annotation { "Feature Type Name" : "Feature", "Feature Type Description" : "" }
export const myFeature = defineFeature(function(context is Context, id is Id, definition is map)
    precondition{}
    {
        {
            var Q0;
            Q0=qCreatedBy(makeId("Top.planeOp"),FACE);
            var sketch = newSketch(context, id + "F0", { "sketchPlane" : qUnion([Q0])});
            skLineSegment(sketch, "E0.bottom", {"start": v(-93.3, 45.8) * mm, "end": v(93.3, 45.8) * mm});
            skLineSegment(sketch, "E0.top", {"start": v(-93.3, -45.8) * mm, "end": v(93.3, -45.8) * mm});
            skLineSegment(sketch, "E0.left", {"start": v(-103.3, 35.8) * mm, "end": v(-103.3, -35.8) * mm});
            skLineSegment(sketch, "E0.right", {"start": v(103.3, 35.8) * mm, "end": v(103.3, -35.8) * mm});
            skPoint(sketch, "E1", {"position": v(-103.3, 0) * mm});
            skPoint(sketch, "E2", {"position": v(0, 45.8) * mm});
            skPoint(sketch, "E3.visualSharp", {"position": v(-103.3, 45.8) * mm});
            skArc(sketch, "E3.filletArc", {"start": v(-93.3, 45.8) * mm, "mid": v(-100.37, 42.87) * mm, "end": v(-103.3, 35.8) * mm});
            skPoint(sketch, "E4.visualSharp", {"position": v(103.3, 45.8) * mm});
            skArc(sketch, "E4.filletArc", {"start": v(103.3, 35.8) * mm, "mid": v(100.37, 42.87) * mm, "end": v(93.3, 45.8) * mm});
            skPoint(sketch, "E5.visualSharp", {"position": v(103.3, -45.8) * mm});
            skArc(sketch, "E5.filletArc", {"start": v(93.3, -45.8) * mm, "mid": v(100.37, -42.87) * mm, "end": v(103.3, -35.8) * mm});
            skPoint(sketch, "E6.visualSharp", {"position": v(-103.3, -45.8) * mm});
            skArc(sketch, "E6.filletArc", {"start": v(-103.3, -35.8) * mm, "mid": v(-100.37, -42.87) * mm, "end": v(-93.3, -45.8) * mm});
            skSolve(sketch);
        }
        {
            var Q0;
            Q0=qCreatedBy(makeId("Top.planeOp"),FACE);
            var sketch = newSketch(context, id + "F1", { "sketchPlane" : qUnion([Q0])});
            skLineSegment(sketch, "E7", {"start": v(-42.83, 13.32) * mm, "end": v(-36.1, 13.32) * mm});
            skLineSegment(sketch, "E8", {"start": v(-36.1, 13.32) * mm, "end": v(-39.45, -1.37) * mm});
            skLineSegment(sketch, "E9", {"start": v(-42.83, 13.32) * mm, "end": v(-46.01, -0.65) * mm});
            skLineSegment(sketch, "E10", {"start": v(-45.48, 8.48) * mm, "end": v(-46.34, 4.71) * mm});
            skLineSegment(sketch, "E11", {"start": v(-53.53, -1.78) * mm, "end": v(-47.43, -1.78) * mm});
            skLineSegment(sketch, "E12", {"start": v(-54.43, -0.65) * mm, "end": v(-53.38, 4) * mm});
            skLineSegment(sketch, "E13", {"start": v(-46.34, 4.71) * mm, "end": v(-52.47, 4.71) * mm});
            skLineSegment(sketch, "E14", {"start": v(-45.48, 8.48) * mm, "end": v(-55.95, 8.48) * mm});
            skLineSegment(sketch, "E15", {"start": v(-44.42, -5.34) * mm, "end": v(-60, -5.34) * mm});
            skLineSegment(sketch, "E16", {"start": v(-60.83, 4.59) * mm, "end": v(-62.4, -2.33) * mm});
            skPoint(sketch, "E17.orphan", {"position": v(-46.57, -3.1) * mm});
            skPoint(sketch, "E18.visualSharp", {"position": v(-59.94, 8.48) * mm});
            skArc(sketch, "E18.filletArc", {"start": v(-55.95, 8.48) * mm, "mid": v(-59.07, 7.38) * mm, "end": v(-60.83, 4.59) * mm});
            skPoint(sketch, "E19.visualSharp", {"position": v(-40.35, -5.34) * mm});
            skArc(sketch, "E19.filletArc", {"start": v(-44.42, -5.34) * mm, "mid": v(-41.24, -4.23) * mm, "end": v(-39.45, -1.37) * mm});
            skPoint(sketch, "E20.visualSharp", {"position": v(-63.09, -5.34) * mm});
            skArc(sketch, "E20.filletArc", {"start": v(-62.4, -2.33) * mm, "mid": v(-61.93, -4.41) * mm, "end": v(-60, -5.34) * mm});
            skPoint(sketch, "E21.visualSharp", {"position": v(-54.7, -1.78) * mm});
            skArc(sketch, "E21.filletArc", {"start": v(-54.43, -0.65) * mm, "mid": v(-54.25, -1.43) * mm, "end": v(-53.53, -1.78) * mm});
            skPoint(sketch, "E22.visualSharp", {"position": v(-46.27, -1.78) * mm});
            skArc(sketch, "E22.filletArc", {"start": v(-47.43, -1.78) * mm, "mid": v(-46.52, -1.47) * mm, "end": v(-46.01, -0.65) * mm});
            skPoint(sketch, "E23.visualSharp", {"position": v(-53.21, 4.71) * mm});
            skArc(sketch, "E23.filletArc", {"start": v(-52.47, 4.71) * mm, "mid": v(-53.05, 4.51) * mm, "end": v(-53.38, 4) * mm});
            skLineSegment(sketch, "E24", {"start": v(-35.57, 8.44) * mm, "end": v(-29.1, 8.44) * mm});
            skLineSegment(sketch, "E25", {"start": v(-24.17, -5.38) * mm, "end": v(-30.7, -5.38) * mm});
            skLineSegment(sketch, "E26", {"start": v(-47.3, -6.65) * mm, "end": v(-42.86, -6.65) * mm});
            skLineSegment(sketch, "E27", {"start": v(-48.81, -11.27) * mm, "end": v(-39.5, -11.27) * mm});
            skLineSegment(sketch, "E28", {"start": v(-35.57, 8.44) * mm, "end": v(-38.1, -2.84) * mm});
            skLineSegment(sketch, "E29", {"start": v(-29.1, 8.44) * mm, "end": v(-32.2, -5.43) * mm});
            skLineSegment(sketch, "E30", {"start": v(-47.3, -6.65) * mm, "end": v(-48.81, -11.27) * mm});
            skLineSegment(sketch, "E31", {"start": v(-27.6, 8.44) * mm, "end": v(-30.7, -5.38) * mm});
            skLineSegment(sketch, "E32", {"start": v(-24.17, -5.38) * mm, "end": v(-21.08, 8.44) * mm});
            skLineSegment(sketch, "E33.trimOffspring", {"start": v(-27.6, 8.44) * mm, "end": v(-21.08, 8.44) * mm});
            skPoint(sketch, "E34.visualSharp", {"position": v(-33.5, -11.27) * mm});
            skArc(sketch, "E34.filletArc", {"start": v(-39.5, -11.27) * mm, "mid": v(-34.82, -9.63) * mm, "end": v(-32.2, -5.43) * mm});
            skPoint(sketch, "E35.visualSharp", {"position": v(-38.95, -6.65) * mm});
            skArc(sketch, "E35.filletArc", {"start": v(-42.86, -6.65) * mm, "mid": v(-39.8, -5.58) * mm, "end": v(-38.1, -2.84) * mm});
            skLineSegment(sketch, "E36", {"start": v(0, 46.06) * mm, "end": v(0, -46.43) * mm, "construction": true});
            skText(sketch, "E37", { "text": "MAVIC PRO", "fontName": "OpenSans-Regular.ttf"});
            const initialGuessF1  = {"E37": [-0.00124, -0.00387, 1, 0, 0.008]};
            skSetInitialGuess(sketch, initialGuessF1);
            skSolve(sketch);
        }
        {
            var Q0;
            Q0=makeQuery(id+"F0.imprint","IMPRINT",FACE,{"disambiguationData":[TD([[makeQuery(id+"F0.imprint","IMPRINT",EDGE,{"derivedFrom":sQuery(id+"F0.wireOp",EDGE,"E0.bottom")}),-1.0]])]});
            extrude(context, id + "F2", {"entities" : qUnion([Q0]), "oppositeDirection" : true, "depth" : 5 * mm, "offsetDistance" : 25 * mm});
        }
        {
            var Q0;
            Q0=makeQuery(id+"F2.opExtrude","CAP_FACE",FACE,{"disambiguationData":[OSD([sQuery(id+"F0.wireOp",EDGE,"E0.bottom"),sQuery(id+"F0.wireOp",EDGE,"E0.top"),sQuery(id+"F0.wireOp",EDGE,"E0.left"),sQuery(id+"F0.wireOp",EDGE,"E0.right"),sQuery(id+"F0.wireOp",EDGE,"E3.filletArc"),sQuery(id+"F0.wireOp",EDGE,"E4.filletArc"),sQuery(id+"F0.wireOp",EDGE,"E5.filletArc"),sQuery(id+"F0.wireOp",EDGE,"E6.filletArc")])],"isStart":true});
            fillet(context, id + "F3", {"entities" : qUnion([Q0]), "radius" : 5 * mm, "tangentPropagation" : true, "allowEdgeOverflow" : false});
        }
        {
            var Q0;
            Q0=qSketchRegion(id+"F1",true);
            extrude(context, id + "F4", {"entities" : qUnion([Q0]), "operationType" : NewBodyOperationType.REMOVE, "oppositeDirection" : true, "depth" : 1 * mm, "offsetDistance" : 25 * mm});
        }
    });